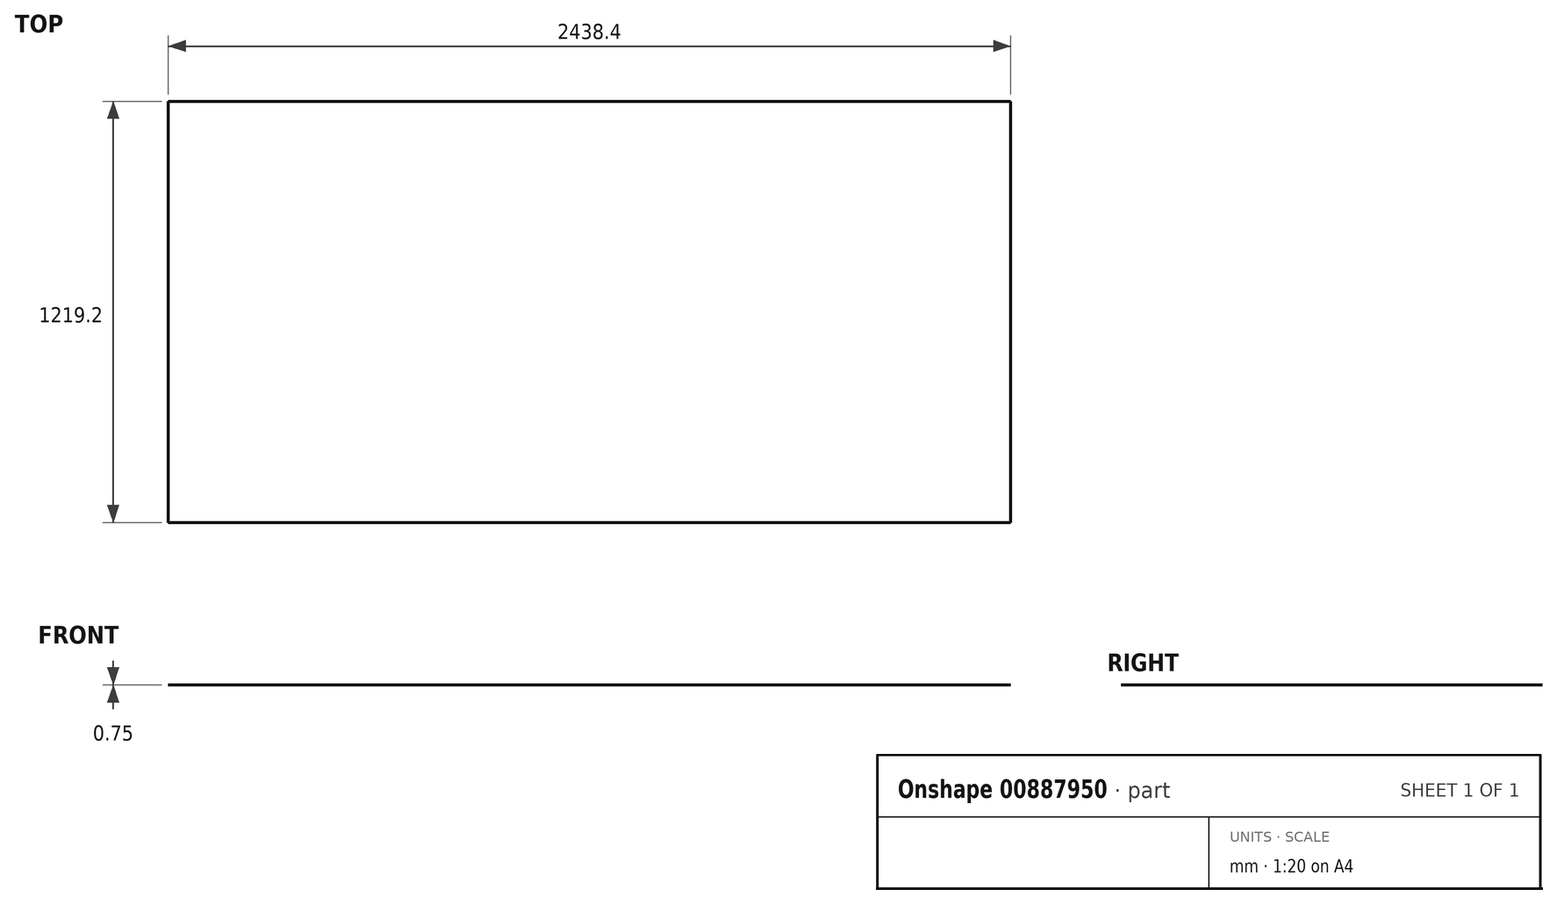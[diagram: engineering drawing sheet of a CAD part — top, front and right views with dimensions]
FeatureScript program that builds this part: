
annotation { "Feature Type Name" : "Feature", "Feature Type Description" : "" }
export const myFeature = defineFeature(function(context is Context, id is Id, definition is map)
    precondition{}
    {
        {
            assignVariable(context, id + "F0", {"name" : "WoodThickness", "anyValue" : .75});
        }
        {
            var Q0;
            Q0=qCreatedBy(makeId("Top.planeOp"),FACE);
            var sketch = newSketch(context, id + "F1", { "sketchPlane" : qUnion([Q0])});
            skLineSegment(sketch, "E0.bottom", {"start": v(1219.2, -609.6) * mm, "end": v(-1219.2, -609.6) * mm});
            skLineSegment(sketch, "E0.top", {"start": v(1219.2, 609.6) * mm, "end": v(-1219.2, 609.6) * mm});
            skLineSegment(sketch, "E0.left", {"start": v(1219.2, -609.6) * mm, "end": v(1219.2, 609.6) * mm});
            skLineSegment(sketch, "E0.right", {"start": v(-1219.2, -609.6) * mm, "end": v(-1219.2, 609.6) * mm});
            skPoint(sketch, "E0.middle", {"position": v(0, 0) * mm});
            skSolve(sketch);
        }
        {
            var Q0;
            Q0 = qSketchRegion(id + "F1", true);
            extrude(context, id + "F2", {"entities" : qUnion([Q0]), "depth" : (getVariable(context, 'WoodThickness')) * mm, "offsetDistance" : 25.4 * mm});
        }
    });
